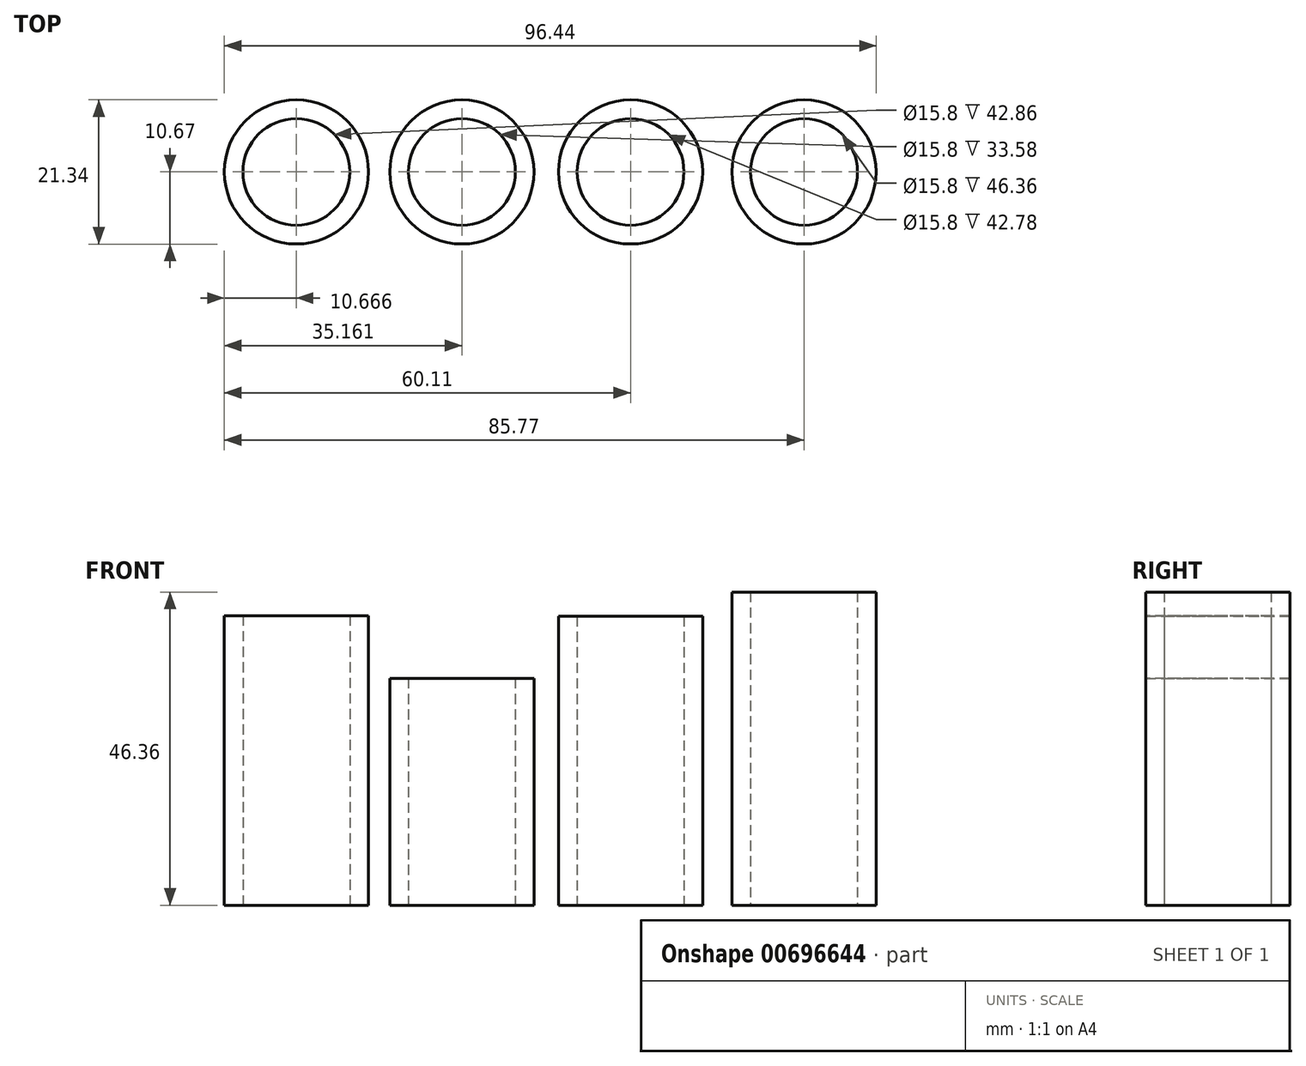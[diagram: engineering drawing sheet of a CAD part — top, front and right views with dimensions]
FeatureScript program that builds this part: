
annotation { "Feature Type Name" : "Feature", "Feature Type Description" : "" }
export const myFeature = defineFeature(function(context is Context, id is Id, definition is map)
    precondition{}
    {
        {
            var Q0;
            Q0=qCreatedBy(makeId("Top.planeOp"),FACE);
            var sketch = newSketch(context, id + "F0", { "sketchPlane" : qUnion([Q0])});
            skCircle(sketch, "E0", {"center": v(0, 0) * mm, "radius": 10.67 * mm});
            skCircle(sketch, "E1", {"center": v(0, 0) * mm, "radius": 7.9 * mm});
            skSolve(sketch);
        }
        {
            var Q0;
            Q0=makeQuery(id+"F0.imprint","IMPRINT",FACE,{"disambiguationData":[TD([[makeQuery(id+"F0.imprint","IMPRINT",EDGE,{"derivedFrom":sQuery(id+"F0.wireOp",EDGE,"E0")}),1.0]])]});
            extrude(context, id + "F1", {"entities" : qUnion([Q0]), "depth" : 42.78 * mm, "offsetDistance" : 25 * mm});
        }
        {
            var Q0;
            Q0=qCreatedBy(makeId("Top.planeOp"),FACE);
            var sketch = newSketch(context, id + "F2", { "sketchPlane" : qUnion([Q0])});
            skCircle(sketch, "E2", {"center": v(-24.95, 0) * mm, "radius": 10.67 * mm});
            skCircle(sketch, "E3", {"center": v(-24.95, 0) * mm, "radius": 7.9 * mm});
            skSolve(sketch);
        }
        {
            var Q0;
            Q0 = qSketchRegion(id + "F2", true);
            extrude(context, id + "F3", {"entities" : qUnion([Q0]), "depth" : 33.58 * mm, "offsetDistance" : 25 * mm});
        }
        {
            var Q0;
            Q0=qCreatedBy(makeId("Top.planeOp"),FACE);
            var sketch = newSketch(context, id + "F4", { "sketchPlane" : qUnion([Q0])});
            skCircle(sketch, "E4", {"center": v(-49.44, 0) * mm, "radius": 10.67 * mm});
            skCircle(sketch, "E5", {"center": v(-49.44, 0) * mm, "radius": 7.9 * mm});
            skSolve(sketch);
        }
        {
            var Q0;
            Q0 = qSketchRegion(id + "F4", true);
            extrude(context, id + "F5", {"entities" : qUnion([Q0]), "depth" : 42.86 * mm, "offsetDistance" : 25 * mm});
        }
        {
            var Q0;
            Q0=qCreatedBy(makeId("Top.planeOp"),FACE);
            var sketch = newSketch(context, id + "F6", { "sketchPlane" : qUnion([Q0])});
            skCircle(sketch, "E6", {"center": v(25.66, 0) * mm, "radius": 10.67 * mm});
            skCircle(sketch, "E7", {"center": v(25.66, 0) * mm, "radius": 7.9 * mm});
            skSolve(sketch);
        }
        {
            var Q0;
            Q0 = qSketchRegion(id + "F6", true);
            extrude(context, id + "F7", {"entities" : qUnion([Q0]), "depth" : 46.36 * mm, "offsetDistance" : 25 * mm});
        }
    });
